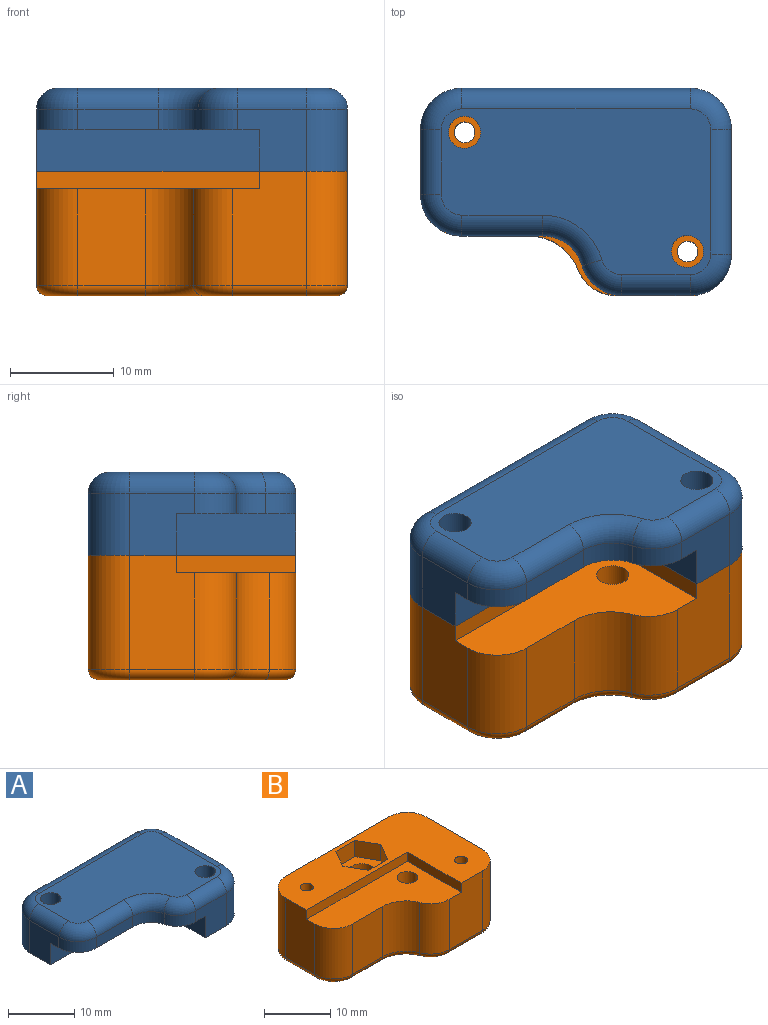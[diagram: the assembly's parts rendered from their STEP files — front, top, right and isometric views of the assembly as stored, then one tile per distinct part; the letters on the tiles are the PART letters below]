
ASSEMBLY  parts=2 mates=1
PART A: 29 faces, bbox 30.7x20.7x8 mm
  f0: plane 6.57x6mm, normal (0,-1,0), area 31.1mm2, adj f2,f3,f8,f11,f14,f24
  f1: plane 26x16mm, normal (0,0,1), area 314.1mm2, adj f16,f17,f18,f19,f20,f21,f22,f23
  f2: plane 21.5x11.5mm, normal (0,0,-1), area 154.2mm2, adj f0,f5,f7,f8,f9,f10,f11,f12
  f3: plane 30x20mm, normal (0,0,-1), area 327.4mm2, adj f0,f4,f5,f6,f7,f8,f13,f14
  f4: plane 22x6mm, normal (0,1,0), area 132mm2, adj f3,f13,f15,f19
  f5: plane 6.25x6mm, normal (-1,0,0), area 30.5mm2, adj f2,f3,f7,f12,f13,f23
  f6: plane 12x6mm, normal (1,0,0), area 72mm2, adj f3,f14,f15,f20
  f7: plane 21.5x4mm, normal (0,-1,0), area 86mm2, adj f2,f3,f5,f8
  f8: plane 11.5x4mm, normal (-1,0,0), area 46mm2, adj f0,f2,f3,f7
  f9: plane 7.75x2mm, normal (0,-1,0), area 15.5mm2, adj f2,f10,f12,f27
  f10: cylinder r=4mm len=3.84mm, axis (0,0,-1), area 10.3mm2, adj f2,f9,f11,f28
  f11: cylinder r=4mm len=3.84mm, axis (0,0,-1), area 10.3mm2, adj f0,f2,f10,f26
  f12: cylinder r=4mm len=4mm, axis (0,0,1), area 12.6mm2, adj f2,f5,f9,f25
  f13: cylinder r=4mm len=6mm, axis (0,0,1), area 37.7mm2, adj f3,f4,f5,f21
  f14: cylinder r=4mm len=6mm, axis (0,0,1), area 37.7mm2, adj f0,f3,f6,f22
  f15: cylinder r=4mm len=6mm, axis (0,0,-1), area 37.7mm2, adj f3,f4,f6,f18
  f16: cylinder r=1.55mm len=8mm, axis (0,0,1), area 77.9mm2, adj f1,f3
  f17: cylinder r=1.55mm len=8mm, axis (0,0,1), area 77.9mm2, adj f1,f3
  f18: torus R=2mm, axis (0,0,1), area 16.2mm2, adj f1,f15,f19,f20
  f19: cylinder r=2mm len=22mm, axis (1,0,0), area 69.1mm2, adj f1,f4,f18,f21
  f20: cylinder r=2mm len=12mm, axis (0,-1,0), area 37.7mm2, adj f1,f6,f18,f22
  f21: torus R=2mm, axis (0,0,1), area 16.2mm2, adj f1,f13,f19,f23
  f22: torus R=2mm, axis (0,0,1), area 16.2mm2, adj f1,f14,f20,f24
  f23: cylinder r=2mm len=6.25mm, axis (0,1,0), area 19.6mm2, adj f1,f5,f21,f25
  f24: cylinder r=2mm len=6.57mm, axis (-1,0,0), area 20.6mm2, adj f0,f1,f22,f26
  f25: torus R=2mm, axis (0,0,1), area 16.2mm2, adj f1,f12,f23,f27
  f26: torus R=2mm, axis (0,0,1), area 13.2mm2, adj f1,f11,f24,f28
  f27: cylinder r=2mm len=7.75mm, axis (1,0,0), area 24.3mm2, adj f1,f9,f25,f28
  f28: torus R=6mm, axis (0,0,1), area 19.1mm2, adj f1,f10,f26,f27
PART B: 45 faces, bbox 30.7x20.7x12 mm
  f0: cylinder r=1.55mm len=7.8mm, axis (0,0,1), area 76mm2, adj f4,f29
  f1: cylinder r=2.05mm len=9mm, axis (0,0,1), area 115.9mm2, adj f3,f22
  f2: plane 11x6.25mm, normal (-1,0,0), area 65.8mm2, adj f4,f6,f10,f30,f33,f37
  f3: plane 28x18mm, normal (0,0,-1), area 363.2mm2, adj f1,f14,f15,f23,f24,f25,f26,f27
  f4: plane 21.5x11.5mm, normal (0,0,1), area 150.6mm2, adj f0,f2,f5,f10,f11,f12,f13,f30
  f5: plane 11x7.11mm, normal (0,-1,0), area 73.7mm2, adj f4,f6,f11,f31,f32,f42
  f6: plane 30x20mm, normal (0,0,1), area 293.7mm2, adj f2,f5,f7,f8,f9,f10,f11,f14
  f7: plane 12x11mm, normal (1,0,0), area 132mm2, adj f6,f8,f32,f38
  f8: cylinder r=4mm len=11mm, axis (0,0,-1), area 69.1mm2, adj f6,f7,f9,f36
  f9: plane 22x11mm, normal (0,1,0), area 242mm2, adj f6,f8,f33,f34
  f10: plane 21.5x1.7mm, normal (0,-1,0), area 36.5mm2, adj f2,f4,f6,f11
  f11: plane 11.5x1.7mm, normal (-1,0,0), area 19.6mm2, adj f4,f5,f6,f10
  f12: plane 9.3x6.5mm, normal (0,-1,0), area 60.5mm2, adj f4,f13,f30,f41
  f13: cylinder r=5mm len=9.3mm, axis (0,0,1), area 55.9mm2, adj f4,f12,f31,f43
  f14: cylinder r=1mm len=12mm, axis (0,0,1), area 75.4mm2, adj f3,f6
  f15: cylinder r=1mm len=12mm, axis (0,0,1), area 75.4mm2, adj f3,f6
  f16: plane 4.04x3mm, normal (0,1,0), area 12.1mm2, adj f6,f17,f21,f22
  f17: plane 3.5x3mm, normal (-0.87,0.5,0), area 12.1mm2, adj f6,f16,f18,f22
  f18: plane 3.5x3mm, normal (-0.87,-0.5,0), area 12.1mm2, adj f6,f17,f19,f22
  f19: plane 4.04x3mm, normal (0,-1,0), area 12.1mm2, adj f6,f18,f20,f22
  f20: plane 3.5x3mm, normal (0.87,-0.5,0), area 12.1mm2, adj f6,f19,f21,f22
  f21: plane 3.5x3mm, normal (0.87,0.5,0), area 12.1mm2, adj f6,f16,f20,f22
  f22: plane 8.08x7mm, normal (0,0,1), area 29.2mm2, adj f1,f16,f17,f18,f19,f20,f21
  f23: plane 3x2.5mm, normal (0.87,0.5,0), area 8.7mm2, adj f3,f24,f28,f29
  f24: plane 3x2.5mm, normal (0.87,-0.5,0), area 8.7mm2, adj f3,f23,f25,f29
  f25: plane 3.46x2.5mm, normal (0,-1,0), area 8.7mm2, adj f3,f24,f26,f29
  f26: plane 3x2.5mm, normal (-0.87,-0.5,0), area 8.7mm2, adj f3,f25,f27,f29
  f27: plane 3x2.5mm, normal (-0.87,0.5,0), area 8.7mm2, adj f3,f26,f28,f29
  f28: plane 3.46x2.5mm, normal (0,1,0), area 8.7mm2, adj f3,f23,f27,f29
  f29: plane 6.93x6mm, normal (0,0,-1), area 23.6mm2, adj f0,f23,f24,f25,f26,f27,f28
  f30: cylinder r=4mm len=9.3mm, axis (0,0,1), area 58.4mm2, adj f2,f4,f12,f39
  f31: cylinder r=4mm len=9.3mm, axis (0,0,1), area 44.7mm2, adj f4,f5,f13,f44
  f32: cylinder r=4mm len=11mm, axis (0,0,1), area 69.1mm2, adj f5,f6,f7,f40
  f33: cylinder r=4mm len=11mm, axis (0,0,1), area 69.1mm2, adj f2,f6,f9,f35
  f34: cylinder r=1mm len=22mm, axis (-1,0,0), area 34.6mm2, adj f3,f9,f35,f36
  f35: torus R=3mm, axis (0,0,1), area 9mm2, adj f3,f33,f34,f37
  f36: torus R=3mm, axis (0,0,1), area 9mm2, adj f3,f8,f34,f38
  f37: cylinder r=1mm len=6.25mm, axis (0,-1,0), area 9.8mm2, adj f2,f3,f35,f39
  f38: cylinder r=1mm len=12mm, axis (0,1,0), area 18.8mm2, adj f3,f7,f36,f40
  f39: torus R=3mm, axis (0,0,1), area 9mm2, adj f3,f30,f37,f41
  f40: torus R=3mm, axis (0,0,1), area 9mm2, adj f3,f32,f38,f42
  f41: cylinder r=1mm len=6.5mm, axis (-1,0,0), area 10.2mm2, adj f3,f12,f39,f43
  f42: cylinder r=1mm len=7.11mm, axis (1,0,0), area 11.2mm2, adj f3,f5,f40,f44
  f43: torus R=6mm, axis (0,0,1), area 10.1mm2, adj f3,f13,f41,f44
  f44: torus R=3mm, axis (0,0,1), area 6.9mm2, adj f3,f31,f42,f43
PLACE A t=(-1.41,11.84,31.62)mm
PLACE B t=(-1.86,10.18,19.62)mm
MATE fastened B.f14 <-> A.f17  axis (0,0,1) through (8.89,4.43,31.62)mm
